# Revit family: Shaker Cabinet - Base Single Door
name_source: partatom
category: Generic Models
revit_build: Autodesk Revit 2018 (Build: 20170223_1515(x64)
units: mm (PartAtom-declared; Revit-internal decimal feet)

## family parameters
Always vertical = Yes
Can host rebar = No
Cut with Voids When Loaded = No
Host = Floor
Part Type = Normal
Room Calculation Point = No
Round Connector Dimension = Use Diameter
Shared = No

## types (1)
- Shaker Cabinet - Base Single Door
    Cabinet Material = <By Category>
    Counter Height = 3' - 0"
    Counter Material = <By Category>
    Counter Top = Yes
    Depth = 2' - 0"
    Door Gap = 0' - 0 1/2"
    Door Height = 2' - 6 1/2"
    Door Material = <By Category>
    Door Panel Material = <By Category>
    Door Width = 2' - 11"
    Height = 2' - 10 1/2"
    Rail Width = 0' - 0"
    Show Center Stile = No
    Show Rails = Yes
    Stile Width = 0' - 0"
    Toe Depth = 0' - 3"
    Toe Height = 0' - 3"
    Width = 3' - 0"

## geometry (parser evidence)
native form markers: Sweep x21
no freeform markers — native parametric forms only
